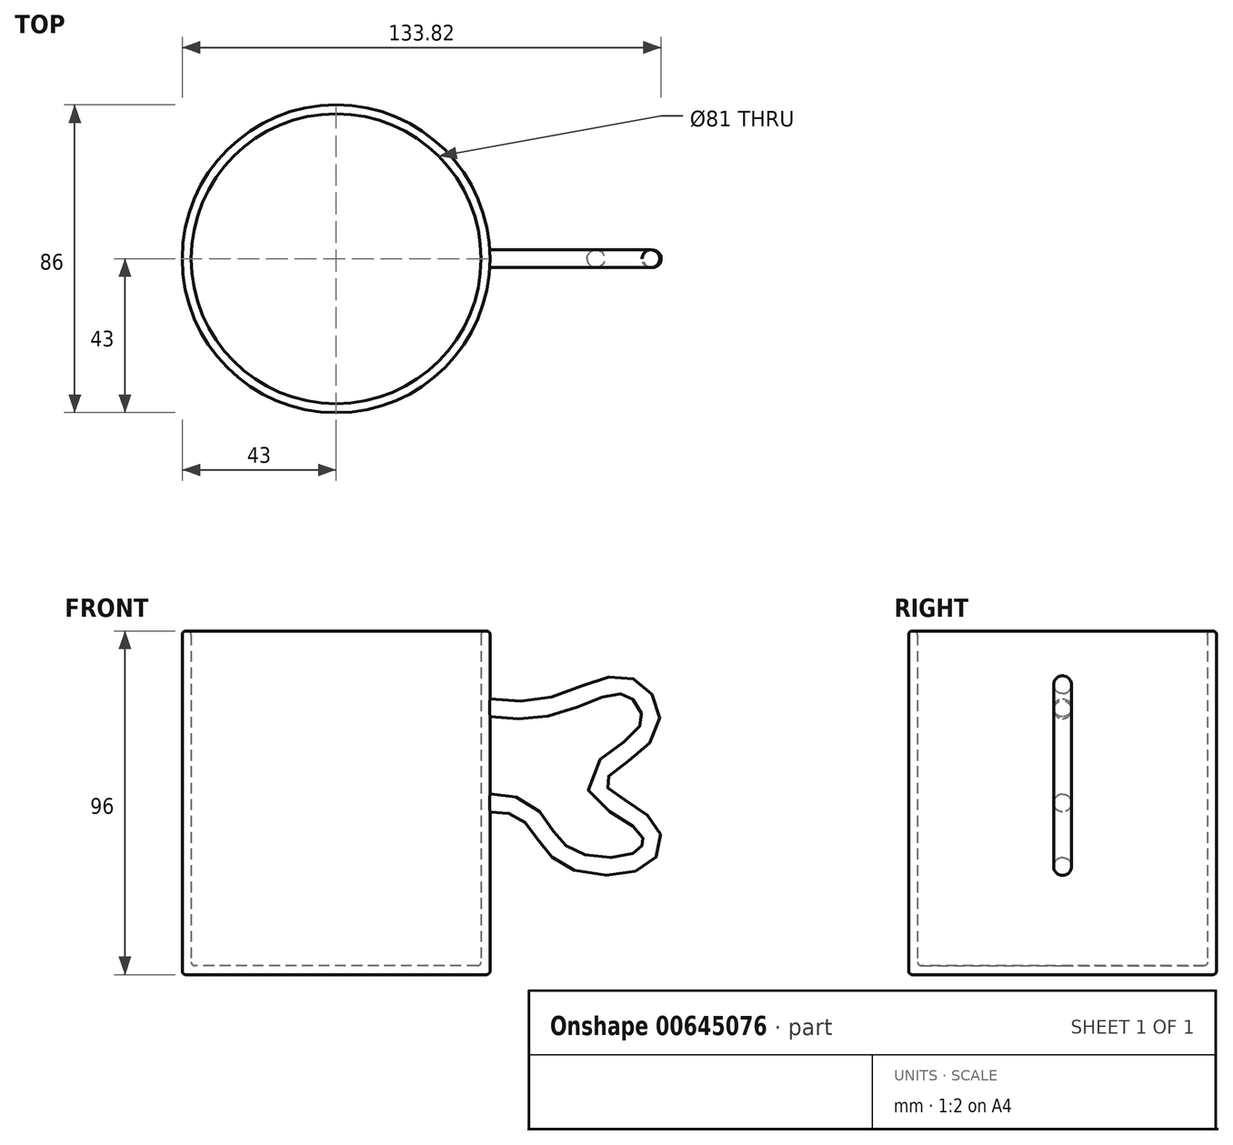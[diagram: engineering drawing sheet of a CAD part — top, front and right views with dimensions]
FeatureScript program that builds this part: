
annotation { "Feature Type Name" : "Feature", "Feature Type Description" : "" }
export const myFeature = defineFeature(function(context is Context, id is Id, definition is map)
    precondition{}
    {
        {
            var Q0;
            Q0=qCreatedBy(makeId("Top.planeOp"),FACE);
            var sketch = newSketch(context, id + "F0", { "sketchPlane" : qUnion([Q0])});
            skCircle(sketch, "E0", {"center": v(0, 0) * mm, "radius": 43 * mm});
            skSolve(sketch);
        }
        {
            var Q0;
            Q0 = qSketchRegion(id + "F0", true);
            extrude(context, id + "F1", {"entities" : qUnion([Q0]), "depth" : 96 * mm, "offsetDistance" : 25 * mm});
        }
        {
            var Q0;
            Q0=qCreatedBy(makeId("Front.planeOp"),FACE);
            var sketch = newSketch(context, id + "F2", { "sketchPlane" : qUnion([Q0])});
            skFitSpline(sketch, "E1", {"points": [v(37.39, 76.81) * mm, v(60.96, 76.81) * mm, v(81.95, 82.17) * mm, v(88.81, 68.03) * mm, v(74.24, 53.67) * mm, v(88.17, 42.1) * mm, v(86.45, 31.18) * mm, v(62.67, 32.03) * mm, v(52.17, 44.25) * mm, v(37.39, 45.96) * mm], "startDerivative": vector(194.17, -21.23) * mm, "endDerivative": vector(-154.08, -14.41) * mm});
            skSolve(sketch);
        }
        {
            var Q0;
            Q0=qCreatedBy(makeId("Right.planeOp"),FACE);
            cPlane(context, id + "F3", {"entities" : qUnion([Q0]), "cplaneType" : CPlaneType.OFFSET, "offset" : 37 * mm, "width" : 150 * mm, "height" : 150 * mm});
        }
        {
            var Q0;
            Q0=qCreatedBy(id+"F3.planeOp",FACE);
            var sketch = newSketch(context, id + "F4", { "sketchPlane" : qUnion([Q0])});
            skCircle(sketch, "E2", {"center": v(0, 75.22) * mm, "radius": 2.5 * mm});
            skSolve(sketch);
        }
        {
            var Q0;
            Q0 = qSketchRegion(id + "F4", true);
            var Q1;
            Q1 = qConstructionFilter(qBodyType(qCreatedBy(id + "F2" ,EDGE), BodyType.WIRE), ConstructionObject.NO);
            sweep(context, id + "F5", {"operationType" : NewBodyOperationType.ADD, "profiles" : qUnion([Q0]), "path" : qUnion([Q1])});
        }
        {
            var Q0;
            Q0=makeQuery(id+"F1.opExtrude","CAP_FACE",FACE,{"disambiguationData":[OSD([sQuery(id+"F0.wireOp",EDGE,"E0")])],"isStart":false});
            shell(context, id + "F6", {"entities" : qUnion([Q0]), "thickness" : 2.5 * mm});
        }
        {
            var Q0;
            {var subQ0=sQuery(id+"F0.wireOp",EDGE,"E0");Q0=makeQuery(id+"F6.opShell","OFFSET_EDGE",EDGE,{"disambiguationData":[OSD([subQ0]),TDD([makeQuery(id+"F1.opExtrude","CAP_EDGE",EDGE,{"disambiguationData":[OSD([subQ0])],"isStart":false})])]});}
            var Q1;
            Q1=makeQuery(id+"F1.opExtrude","CAP_EDGE",EDGE,{"disambiguationData":[OSD([sQuery(id+"F0.wireOp",EDGE,"E0")])],"isStart":false});
            var Q2;
            Q2=makeQuery(id+"F1.opExtrude","CAP_EDGE",EDGE,{"disambiguationData":[OSD([sQuery(id+"F0.wireOp",EDGE,"E0")])],"isStart":true});
            var Q3;
            {var subQ0=sQuery(id+"F0.wireOp",EDGE,"E0");Q3=makeQuery(id+"F6.opShell","OFFSET_EDGE",EDGE,{"disambiguationData":[OSD([subQ0]),TDD([makeQuery(id+"F1.opExtrude","CAP_EDGE",EDGE,{"disambiguationData":[OSD([subQ0])],"isStart":true})])]});}
            fillet(context, id + "F7", {"entities" : qUnion([Q0, Q1, Q2, Q3]), "radius" : 1 * mm, "tangentPropagation" : true, "allowEdgeOverflow" : false});
        }
    });
